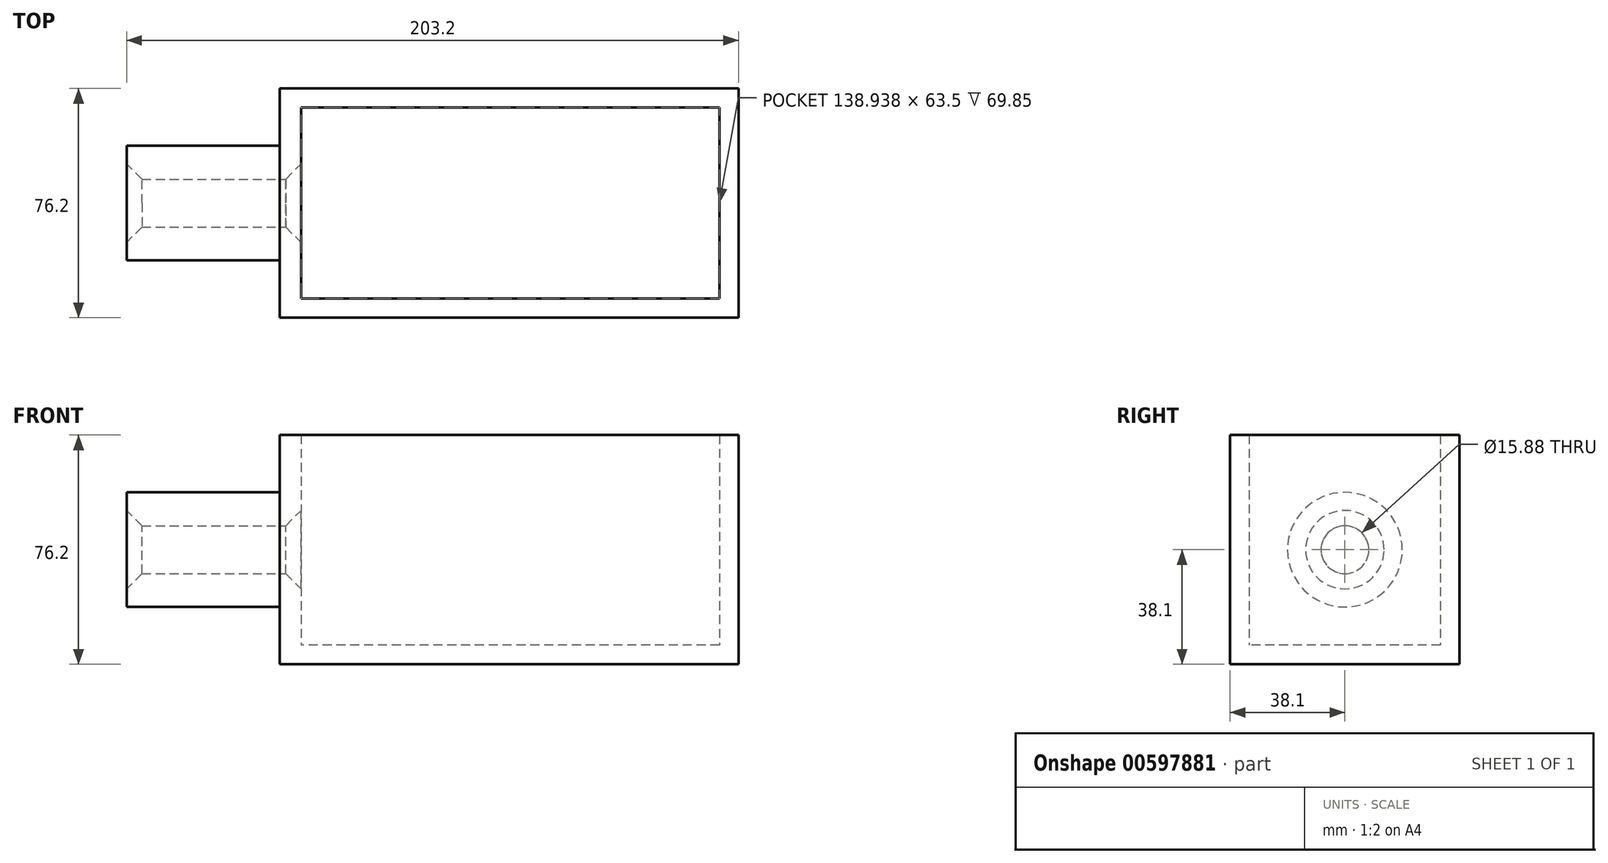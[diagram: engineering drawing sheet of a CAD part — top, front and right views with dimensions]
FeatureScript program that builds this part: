
annotation { "Feature Type Name" : "Feature", "Feature Type Description" : "" }
export const myFeature = defineFeature(function(context is Context, id is Id, definition is map)
    precondition{}
    {
        {
            var Q0;
            Q0=qCreatedBy(makeId("Top.planeOp"),FACE);
            var sketch = newSketch(context, id + "F0", { "sketchPlane" : qUnion([Q0])});
            skLineSegment(sketch, "E0.bottom", {"start": v(-76.2, 38.1) * mm, "end": v(76.2, 38.1) * mm});
            skLineSegment(sketch, "E0.top", {"start": v(-76.2, -38.1) * mm, "end": v(76.2, -38.1) * mm});
            skLineSegment(sketch, "E0.left", {"start": v(-76.2, 38.1) * mm, "end": v(-76.2, -38.1) * mm});
            skLineSegment(sketch, "E0.right", {"start": v(76.2, 38.1) * mm, "end": v(76.2, -38.1) * mm});
            skPoint(sketch, "E0.middle", {"position": v(0, 0) * mm});
            skSolve(sketch);
        }
        {
            var Q0;
            Q0 = qSketchRegion(id + "F0", true);
            extrude(context, id + "F1", {"entities" : qUnion([Q0]), "depth" : 6.35 * mm, "offsetDistance" : 25.4 * mm});
        }
        {
            var Q0;
            Q0=makeQuery(id+"F1.opExtrude","CAP_FACE",FACE,{"disambiguationData":[OSD([sQuery(id+"F0.wireOp",EDGE,"E0.bottom"),sQuery(id+"F0.wireOp",EDGE,"E0.top"),sQuery(id+"F0.wireOp",EDGE,"E0.left"),sQuery(id+"F0.wireOp",EDGE,"E0.right")])],"isStart":false});
            var sketch = newSketch(context, id + "F2", { "sketchPlane" : qUnion([Q0])});
            skLineSegment(sketch, "E1.bottom", {"start": v(-76.2, 38.1) * mm, "end": v(-69.09, 38.1) * mm});
            skLineSegment(sketch, "E1.top", {"start": v(-76.2, -38.1) * mm, "end": v(-69.09, -38.1) * mm});
            skLineSegment(sketch, "E1.left", {"start": v(-76.2, 38.1) * mm, "end": v(-76.2, -38.1) * mm});
            skLineSegment(sketch, "E1.right", {"start": v(-69.09, 38.1) * mm, "end": v(-69.09, -38.1) * mm});
            skLineSegment(sketch, "E2.bottom", {"start": v(-69.09, 38.1) * mm, "end": v(76.2, 38.1) * mm});
            skLineSegment(sketch, "E2.top", {"start": v(-69.09, 31.75) * mm, "end": v(76.2, 31.75) * mm});
            skLineSegment(sketch, "E2.left", {"start": v(-69.09, 38.1) * mm, "end": v(-69.09, 31.75) * mm});
            skLineSegment(sketch, "E2.right", {"start": v(76.2, 38.1) * mm, "end": v(76.2, 31.75) * mm});
            skLineSegment(sketch, "E3.bottom", {"start": v(76.2, 31.75) * mm, "end": v(69.85, 31.75) * mm});
            skLineSegment(sketch, "E3.top", {"start": v(76.2, -38.1) * mm, "end": v(69.85, -38.1) * mm});
            skLineSegment(sketch, "E3.left", {"start": v(76.2, 31.75) * mm, "end": v(76.2, -38.1) * mm});
            skLineSegment(sketch, "E3.right", {"start": v(69.85, 31.75) * mm, "end": v(69.85, -38.1) * mm});
            skLineSegment(sketch, "E4.bottom", {"start": v(69.85, -38.1) * mm, "end": v(-69.09, -38.1) * mm});
            skLineSegment(sketch, "E4.top", {"start": v(69.85, -31.75) * mm, "end": v(-69.09, -31.75) * mm});
            skLineSegment(sketch, "E4.left", {"start": v(69.85, -38.1) * mm, "end": v(69.85, -31.75) * mm});
            skLineSegment(sketch, "E4.right", {"start": v(-69.09, -38.1) * mm, "end": v(-69.09, -31.75) * mm});
            skSolve(sketch);
        }
        {
            var Q0;
            Q0 = qSketchRegion(id + "F2", true);
            extrude(context, id + "F3", {"entities" : qUnion([Q0]), "operationType" : NewBodyOperationType.ADD, "depth" : 69.85 * mm, "offsetDistance" : 25.4 * mm});
        }
        {
            var Q0;
            Q0=makeQuery(id+"F3.boolean.opBoolean","MERGE",FACE,{"derivedFrom":[makeQuery(id+"F1.opExtrude","SWEPT_FACE",FACE,{"disambiguationData":[OSD([sQuery(id+"F0.wireOp",EDGE,"E0.left")])]}),makeQuery(id+"F3.opExtrude","SWEPT_FACE",FACE,{"disambiguationData":[OSD([sQuery(id+"F2.wireOp",EDGE,"E1.left")])]})]});
            var sketch = newSketch(context, id + "F4", { "sketchPlane" : qUnion([Q0])});
            skCircle(sketch, "E5", {"center": v(0, 38.1) * mm, "radius": 19.05 * mm});
            skPoint(sketch, "E5.centerSnap0", {"position": v(-38.1, 38.1) * mm});
            skCircle(sketch, "E6", {"center": v(0, 38.1) * mm, "radius": 7.94 * mm});
            skSolve(sketch);
        }
        {
            var Q0;
            Q0 = qSketchRegion(id + "F4", true);
            extrude(context, id + "F5", {"entities" : qUnion([Q0]), "operationType" : NewBodyOperationType.ADD, "depth" : 50.8 * mm, "offsetDistance" : 25.4 * mm});
        }
        {
            var Q0;
            Q0=makeQuery(id+"F5.boolean.opBoolean","SPLIT",FACE,{"disambiguationData":[TD([makeQuery(id+"F5.opExtrude","SWEPT_FACE",FACE,{"disambiguationData":[OSD([sQuery(id+"F4.wireOp",EDGE,"E6")])]})])],"derivedFrom":makeQuery(id+"F3.boolean.opBoolean","MERGE",FACE,{"derivedFrom":[makeQuery(id+"F1.opExtrude","SWEPT_FACE",FACE,{"disambiguationData":[OSD([sQuery(id+"F0.wireOp",EDGE,"E0.left")])]}),makeQuery(id+"F3.opExtrude","SWEPT_FACE",FACE,{"disambiguationData":[OSD([sQuery(id+"F2.wireOp",EDGE,"E1.left")])]})]})});
            var sketch = newSketch(context, id + "F6", { "sketchPlane" : qUnion([Q0])});
            skCircle(sketch, "E7", {"center": v(0, 38.1) * mm, "radius": 7.94 * mm});
            skPoint(sketch, "E7.first.point", {"position": v(-7.55, 40.55) * mm});
            skPoint(sketch, "E7.second.point", {"position": v(0, 30.16) * mm});
            skPoint(sketch, "E7.third.point", {"position": v(7.22, 41.4) * mm});
            skSolve(sketch);
        }
        {
            var Q0;
            Q0 = qSketchRegion(id + "F6", true);
            extrude(context, id + "F7", {"entities" : qUnion([Q0]), "operationType" : NewBodyOperationType.REMOVE, "oppositeDirection" : true, "depth" : 7.62 * mm, "offsetDistance" : 25.4 * mm});
        }
        {
            var Q0;
            Q0=makeQuery(id+"F7.boolean.opBoolean","INTERSECT",EDGE,{"derivedFrom":[makeQuery(id+"F3.opExtrude","SWEPT_FACE",FACE,{"disambiguationData":[OSD([sQuery(id+"F2.wireOp",EDGE,"E1.right")])]}),makeQuery(id+"F7.opExtrude","SWEPT_FACE",FACE,{"disambiguationData":[OSD([sQuery(id+"F6.wireOp",EDGE,"E7")])]})]});
            chamfer(context, id + "F8", {"entities" : qUnion([Q0]), "width" : 5.08 * mm, "tangentPropagation" : true});
        }
        {
            var Q0;
            Q0=makeQuery(id+"F5.opExtrude","CAP_EDGE",EDGE,{"disambiguationData":[OSD([sQuery(id+"F4.wireOp",EDGE,"E6")])],"isStart":false});
            chamfer(context, id + "F9", {"entities" : qUnion([Q0]), "width" : 5.08 * mm, "tangentPropagation" : true});
        }
    });
